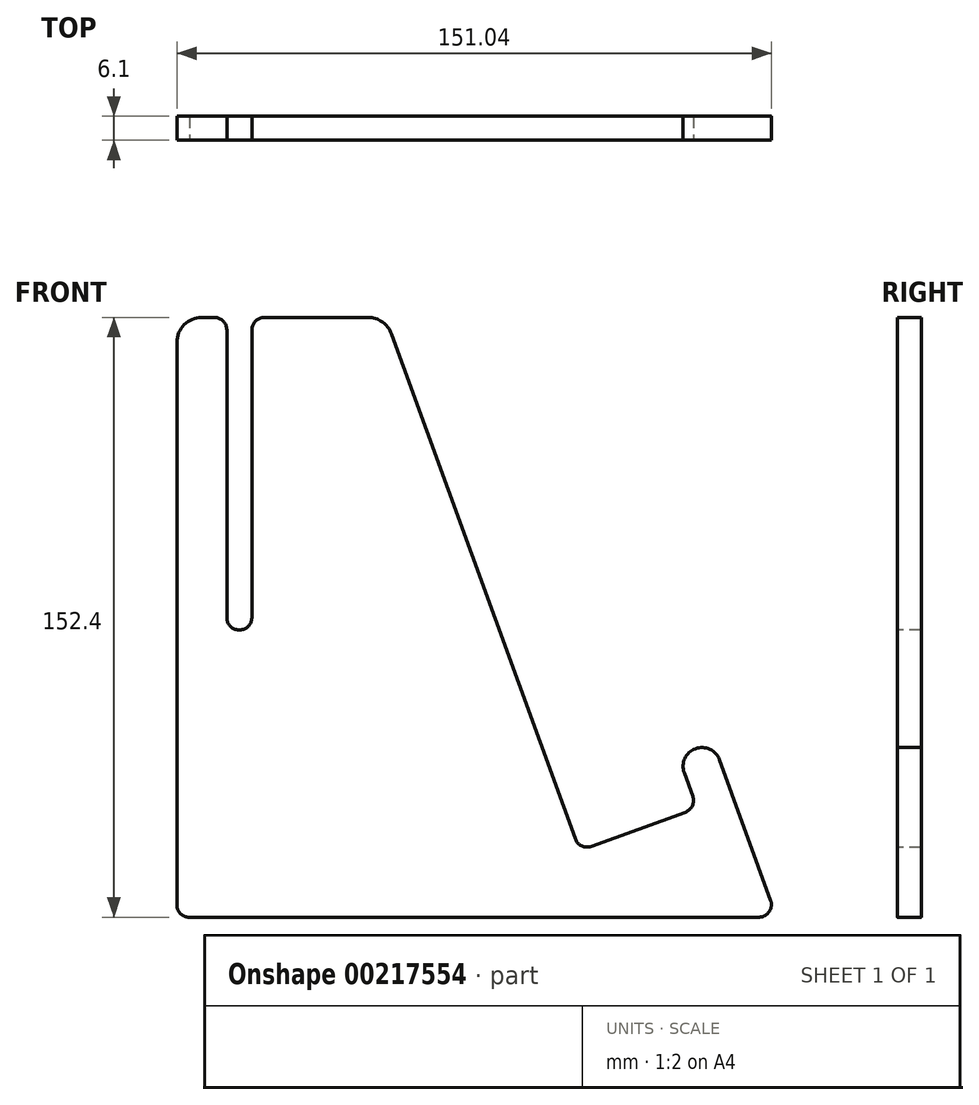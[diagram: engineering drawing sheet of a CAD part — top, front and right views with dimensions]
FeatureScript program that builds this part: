
annotation { "Feature Type Name" : "Feature", "Feature Type Description" : "" }
export const myFeature = defineFeature(function(context is Context, id is Id, definition is map)
    precondition{}
    {
        {
            var Q0;
            Q0=qCreatedBy(makeId("Front.planeOp"),FACE);
            var sketch = newSketch(context, id + "F0", { "sketchPlane" : qUnion([Q0])});
            skLineSegment(sketch, "E0", {"start": v(-150.9, 152.97) * mm, "end": v(-147.73, 152.97) * mm});
            skLineSegment(sketch, "E1", {"start": v(-102.72, 148.8) * mm, "end": v(-56.02, 20.46) * mm});
            skLineSegment(sketch, "E2", {"start": v(-51.95, 18.57) * mm, "end": v(-28.08, 27.25) * mm});
            skLineSegment(sketch, "E3", {"start": v(-157.25, 146.62) * mm, "end": v(-157.25, 3.65) * mm});
            skLineSegment(sketch, "E4", {"start": v(-144.55, 76.64) * mm, "end": v(-144.55, 149.8) * mm});
            skLineSegment(sketch, "E5", {"start": v(-138.2, 149.8) * mm, "end": v(-138.2, 76.64) * mm});
            skLineSegment(sketch, "E6", {"start": v(-154.08, 0.57) * mm, "end": v(-9.39, 0.57) * mm});
            skLineSegment(sketch, "E7", {"start": v(-26.18, 31.32) * mm, "end": v(-28.35, 37.29) * mm});
            skPoint(sketch, "E8.visualSharp", {"position": v(-4.85, 0.57) * mm});
            skPoint(sketch, "E9.visualSharp", {"position": v(-157.25, 0.57) * mm});
            skArc(sketch, "E9.filletArc", {"start": v(-157.25, 3.65) * mm, "mid": v(-156.32, 1.44) * mm, "end": v(-154.08, 0.57) * mm});
            skPoint(sketch, "E10.visualSharp", {"position": v(-157.25, 152.97) * mm});
            skArc(sketch, "E10.filletArc", {"start": v(-150.9, 152.97) * mm, "mid": v(-155.4, 151.11) * mm, "end": v(-157.25, 146.62) * mm});
            skPoint(sketch, "E11.visualSharp", {"position": v(-104.25, 152.97) * mm});
            skArc(sketch, "E11.filletArc", {"start": v(-102.72, 148.8) * mm, "mid": v(-105.05, 151.82) * mm, "end": v(-108.7, 152.97) * mm});
            skPoint(sketch, "E12.visualSharp", {"position": v(-54.93, 17.48) * mm});
            skArc(sketch, "E12.filletArc", {"start": v(-56.02, 20.46) * mm, "mid": v(-54.38, 18.67) * mm, "end": v(-51.95, 18.57) * mm});
            skPoint(sketch, "E13.visualSharp", {"position": v(-25.1, 28.34) * mm});
            skArc(sketch, "E13.filletArc", {"start": v(-28.08, 27.25) * mm, "mid": v(-26.29, 28.9) * mm, "end": v(-26.18, 31.32) * mm});
            skLineSegment(sketch, "E14.0", {"start": v(-6.4, 4.83) * mm, "end": v(-19.4, 40.55) * mm});
            skArc(sketch, "E15.filletArc", {"start": v(-9.39, 0.57) * mm, "mid": v(-6.79, 1.92) * mm, "end": v(-6.4, 4.83) * mm});
            skArc(sketch, "E16", {"start": v(-19.4, 40.55) * mm, "mid": v(-25.5, 43.4) * mm, "end": v(-28.35, 37.29) * mm});
            skLineSegment(sketch, "E17", {"start": v(-141.5, 73.6) * mm, "end": v(-141.25, 73.6) * mm});
            skLineSegment(sketch, "E18.trimOffspring", {"start": v(-135.03, 152.97) * mm, "end": v(-108.7, 152.97) * mm});
            skPoint(sketch, "E19.visualSharp", {"position": v(-144.55, 73.6) * mm});
            skArc(sketch, "E19.filletArc", {"start": v(-144.55, 76.64) * mm, "mid": v(-143.66, 74.49) * mm, "end": v(-141.5, 73.6) * mm});
            skPoint(sketch, "E20.visualSharp", {"position": v(-138.2, 73.6) * mm});
            skArc(sketch, "E20.filletArc", {"start": v(-141.25, 73.6) * mm, "mid": v(-139.1, 74.49) * mm, "end": v(-138.2, 76.64) * mm});
            skPoint(sketch, "E21.visualSharp", {"position": v(-144.55, 152.97) * mm});
            skArc(sketch, "E21.filletArc", {"start": v(-144.55, 149.8) * mm, "mid": v(-145.48, 152.04) * mm, "end": v(-147.73, 152.97) * mm});
            skPoint(sketch, "E22.visualSharp", {"position": v(-138.2, 152.97) * mm});
            skArc(sketch, "E22.filletArc", {"start": v(-135.03, 152.97) * mm, "mid": v(-137.27, 152.04) * mm, "end": v(-138.2, 149.8) * mm});
            skSolve(sketch);
        }
        {
            var Q0;
            Q0=makeQuery(id+"F0.imprint","IMPRINT",FACE,{"disambiguationData":[TD([[makeQuery(id+"F0.imprint","IMPRINT",EDGE,{"derivedFrom":sQuery(id+"F0.wireOp",EDGE,"E0")}),-1.0]])]});
            extrude(context, id + "F1", {"entities" : qUnion([Q0]), "oppositeDirection" : true, "depth" : 6.1 * mm});
        }
    });
